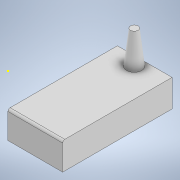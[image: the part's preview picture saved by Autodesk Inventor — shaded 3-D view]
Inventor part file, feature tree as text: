
AUTODESK INVENTOR PART (.ipt)
format: ipt  version: 2020.1 (Build 241239000, 239)  size: 126,976 bytes
history: native  units: mm
features: sketch x5, extrude x2, fillet x1, plane x1, loft x1
ambient origin geometry x8: Origin, YZ Plane, XZ Plane, XY Plane, X Axis, Y Axis, Z Axis, Center Point
bodies: Solid1 (feature_tree)
feature tree (10):
  extrude  "Extrusion1"  Depth=2.0mm
  fillet  "Fillet1"  Radius=100.0mm
  plane  "Work Plane1"
  sketch  "Sketch2"  dims[d4=50.0mm d5=30.0mm]
  loft  "Loft1"
  extrude  "Extrusion2"  TaperAngle=0.0deg  [1 undecoded]
  sketch  "Sketch1"  dims[d0=25.0mm d1=0.0mm d2=2.0mm d3=100.0mm]
  sketch  "Sketch3"  dims[d6=0.0mm d7=90.0deg d8=0.0mm d9=90.0deg]
  sketch  "Sketch4"  dims[d10=10.0mm]
  sketch  "Sketch5"  dims[d11=10.0mm d12=5.0mm d13=30.0mm d15=20.0mm d16=20.0mm d18=20.0mm d21=5.0mm d22=0.0mm]
note: 1 required parameter value undecoded (feature->parameter linkage not recoverable at this tier; creation-order binding heuristic only, values carry confidence <= 0.55)
